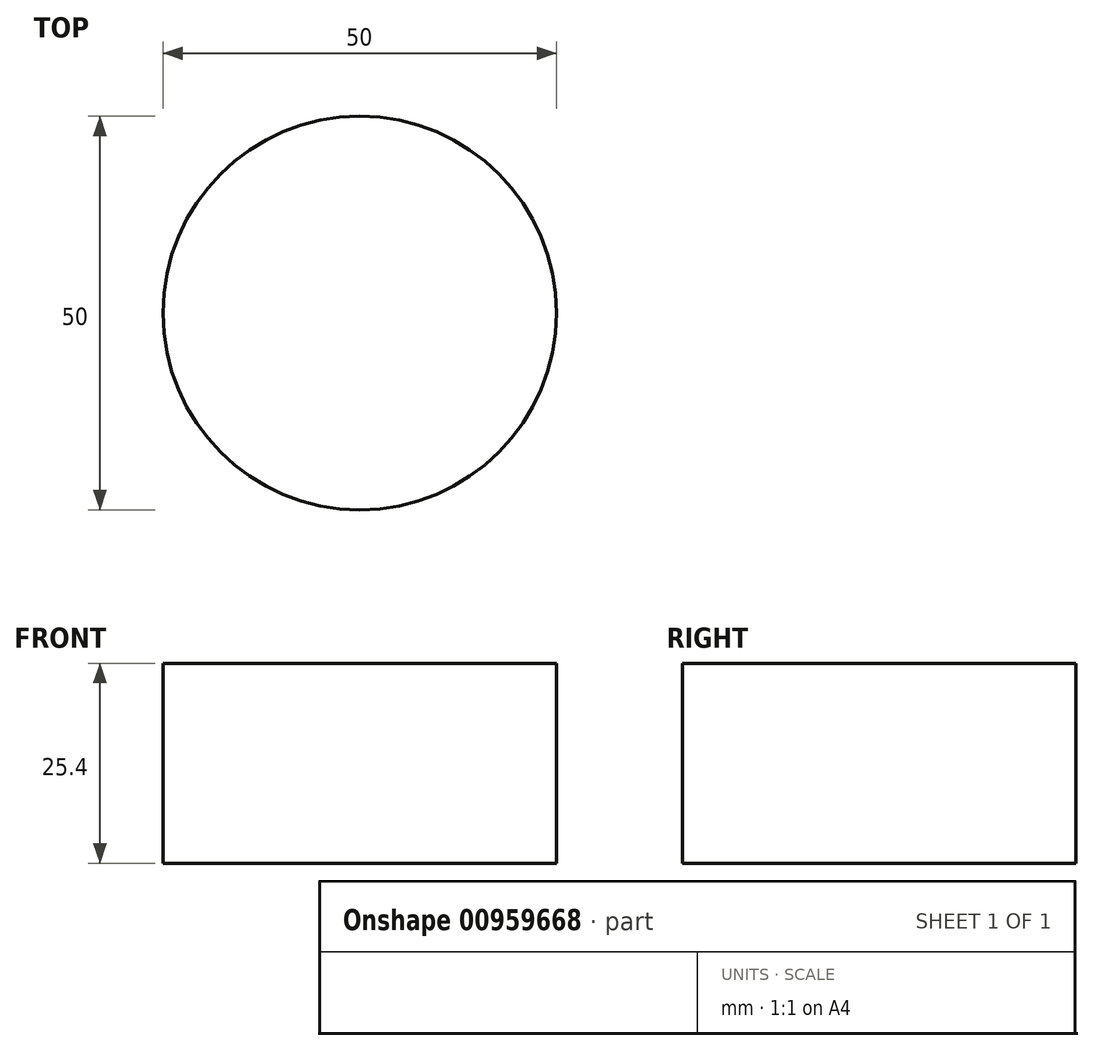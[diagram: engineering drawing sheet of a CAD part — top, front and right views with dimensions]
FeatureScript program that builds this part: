
annotation { "Feature Type Name" : "Feature", "Feature Type Description" : "" }
export const myFeature = defineFeature(function(context is Context, id is Id, definition is map)
    precondition{}
    {
        {
            var Q0;
            Q0=qCreatedBy(makeId("Top.planeOp"),FACE);
            var sketch = newSketch(context, id + "F0", { "sketchPlane" : qUnion([Q0])});
            skCircle(sketch, "E0", {"center": v(0, 0) * mm, "radius": 25 * mm});
            skSolve(sketch);
        }
        {
            var Q0;
            Q0=makeQuery(id+"F0.imprint","IMPRINT",FACE,{"disambiguationData":[TD([[makeQuery(id+"F0.imprint","IMPRINT",EDGE,{"derivedFrom":sQuery(id+"F0.wireOp",EDGE,"E0")}),1.0]])]});
            extrude(context, id + "F1", {"entities" : qUnion([Q0]), "endBound" : BoundingType.SYMMETRIC, "depth" : 25.4 * mm, "offsetDistance" : 25.4 * mm});
        }
    });
